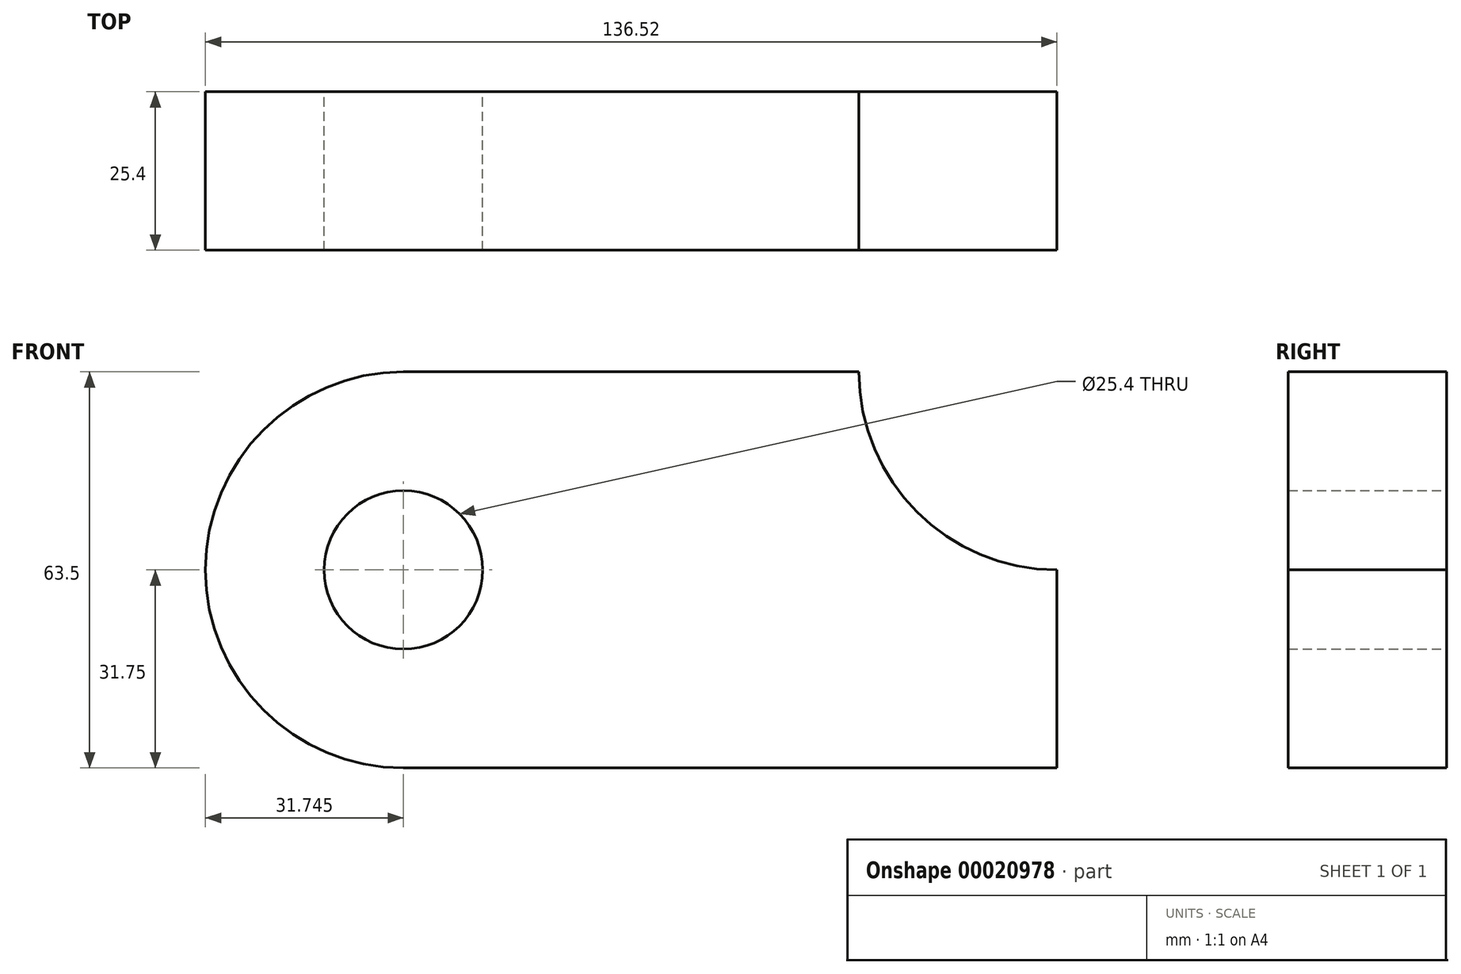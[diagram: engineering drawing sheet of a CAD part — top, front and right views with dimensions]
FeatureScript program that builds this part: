
annotation { "Feature Type Name" : "Feature", "Feature Type Description" : "" }
export const myFeature = defineFeature(function(context is Context, id is Id, definition is map)
    precondition{}
    {
        {
            var Q0;
            Q0=qCreatedBy(makeId("Front.planeOp"),FACE);
            var sketch = newSketch(context, id + "F0", { "sketchPlane" : qUnion([Q0])});
            skLineSegment(sketch, "E0.bottom", {"start": v(0, 0) * mm, "end": v(-104.78, 0) * mm});
            skLineSegment(sketch, "E0.top", {"start": v(0, 63.5) * mm, "end": v(-104.77, 63.5) * mm});
            skLineSegment(sketch, "E0.left", {"start": v(0, 0) * mm, "end": v(0, 63.5) * mm});
            skLineSegment(sketch, "E0.right", {"start": v(-104.78, 0) * mm, "end": v(-104.77, 63.5) * mm});
            skCircle(sketch, "E1", {"center": v(-104.77, 31.75) * mm, "radius": 31.75 * mm});
            skCircle(sketch, "E2", {"center": v(-104.77, 31.75) * mm, "radius": 12.7 * mm});
            skCircle(sketch, "E3", {"center": v(0, 63.5) * mm, "radius": 31.75 * mm});
            skSolve(sketch);
        }
        {
            var Q0;
            {var subQ4=sQuery(id+"F0.wireOp",EDGE,"E0.bottom");Q0=makeQuery(id+"F0.imprint","IMPRINT",FACE,{"disambiguationData":[TD([[makeQuery(id+"F0.imprint","IMPRINT",EDGE,{"derivedFrom":subQ4}),-1.0]])]});}
            var Q1;
            {var subQ0=sQuery(id+"F0.wireOp",EDGE,"E2");var subQ1=sQuery(id+"F0.wireOp",EDGE,"E0.right");var subQ3=makeQuery(id+"F0.imprint","INTERSECT",VERTEX,{"disambiguationData":[OD(0.0)],"derivedFrom":[subQ1,subQ0]});Q1=makeQuery(id+"F0.imprint","IMPRINT",FACE,{"disambiguationData":[TD([[makeQuery(id+"F0.imprint","IMPRINT",EDGE,{"disambiguationData":[TD([[subQ3,-1.0]])],"derivedFrom":subQ0}),-1.0]])]});}
            var Q2;
            {var subQ0=sQuery(id+"F0.wireOp",EDGE,"E2");var subQ1=sQuery(id+"F0.wireOp",EDGE,"E0.right");var subQ3=makeQuery(id+"F0.imprint","INTERSECT",VERTEX,{"disambiguationData":[OD(0.0)],"derivedFrom":[subQ1,subQ0]});Q2=makeQuery(id+"F0.imprint","IMPRINT",FACE,{"disambiguationData":[TD([[makeQuery(id+"F0.imprint","IMPRINT",EDGE,{"disambiguationData":[TD([[subQ3,1.0]])],"derivedFrom":subQ0}),-1.0]])]});}
            extrude(context, id + "F1", {"entities" : qUnion([Q0, Q1, Q2]), "depth" : 25.4 * mm});
        }
    });
